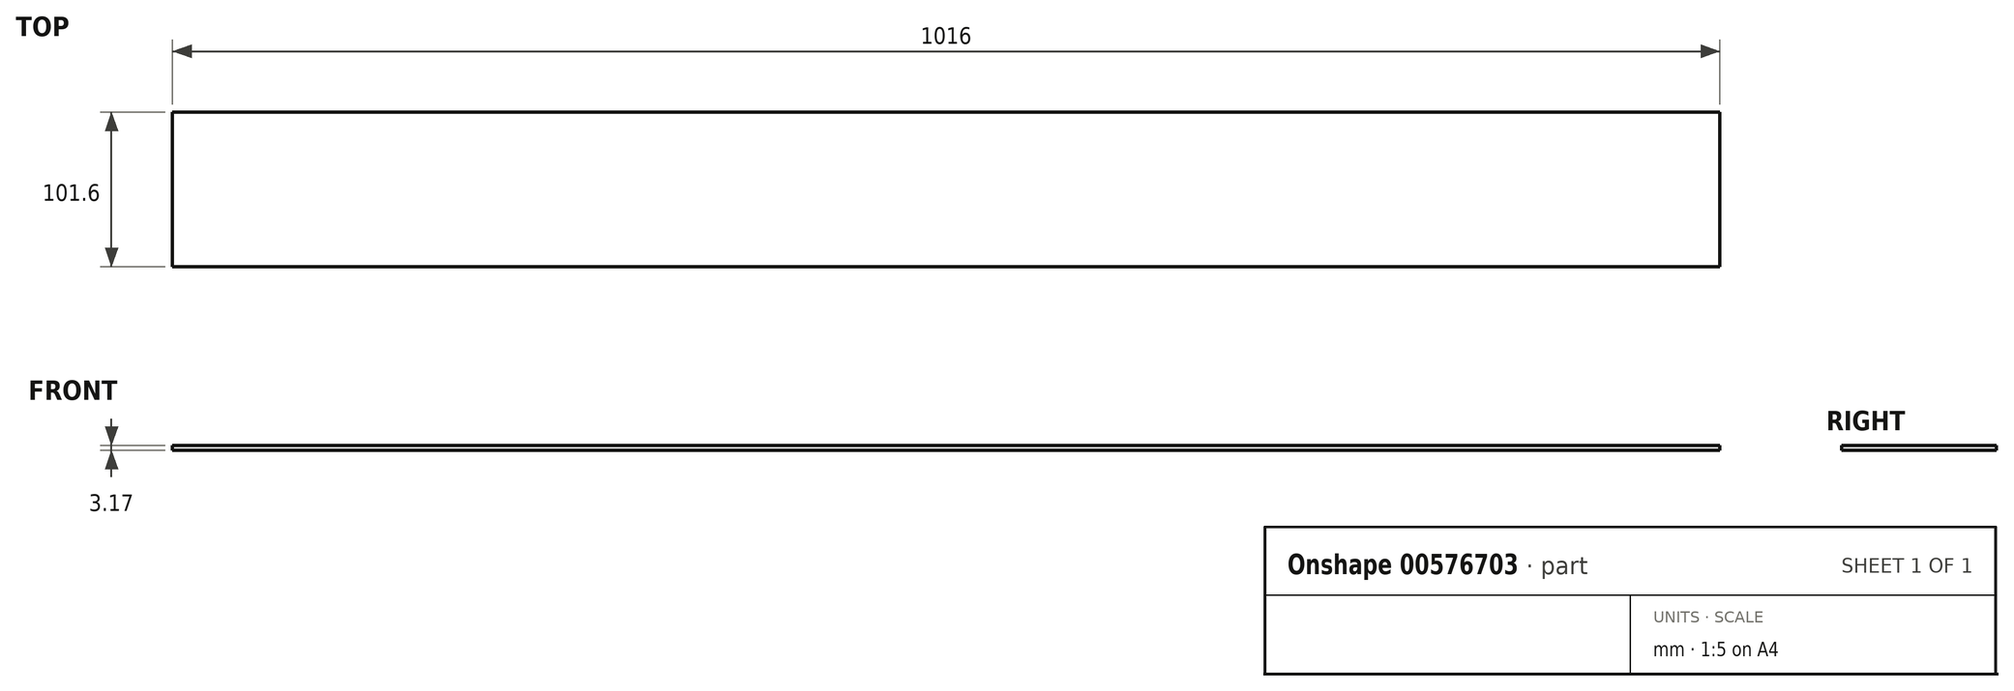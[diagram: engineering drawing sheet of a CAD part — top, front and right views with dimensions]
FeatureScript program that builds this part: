
annotation { "Feature Type Name" : "Feature", "Feature Type Description" : "" }
export const myFeature = defineFeature(function(context is Context, id is Id, definition is map)
    precondition{}
    {
        {
            var Q0;
            Q0=qCreatedBy(makeId("Top.planeOp"),FACE);
            var sketch = newSketch(context, id + "F0", { "sketchPlane" : qUnion([Q0])});
            skLineSegment(sketch, "E0.bottom", {"start": v(508, 50.8) * mm, "end": v(-508, 50.8) * mm});
            skLineSegment(sketch, "E0.top", {"start": v(508, -50.8) * mm, "end": v(-508, -50.8) * mm});
            skLineSegment(sketch, "E0.left", {"start": v(508, 50.8) * mm, "end": v(508, -50.8) * mm});
            skLineSegment(sketch, "E0.right", {"start": v(-508, 50.8) * mm, "end": v(-508, -50.8) * mm});
            skPoint(sketch, "E0.middle", {"position": v(0, 0) * mm});
            skSolve(sketch);
        }
        {
            var Q0;
            Q0 = qSketchRegion(id + "F0", true);
            extrude(context, id + "F1", {"entities" : qUnion([Q0]), "depth" : 3.17 * mm, "offsetDistance" : 25.4 * mm});
        }
    });
